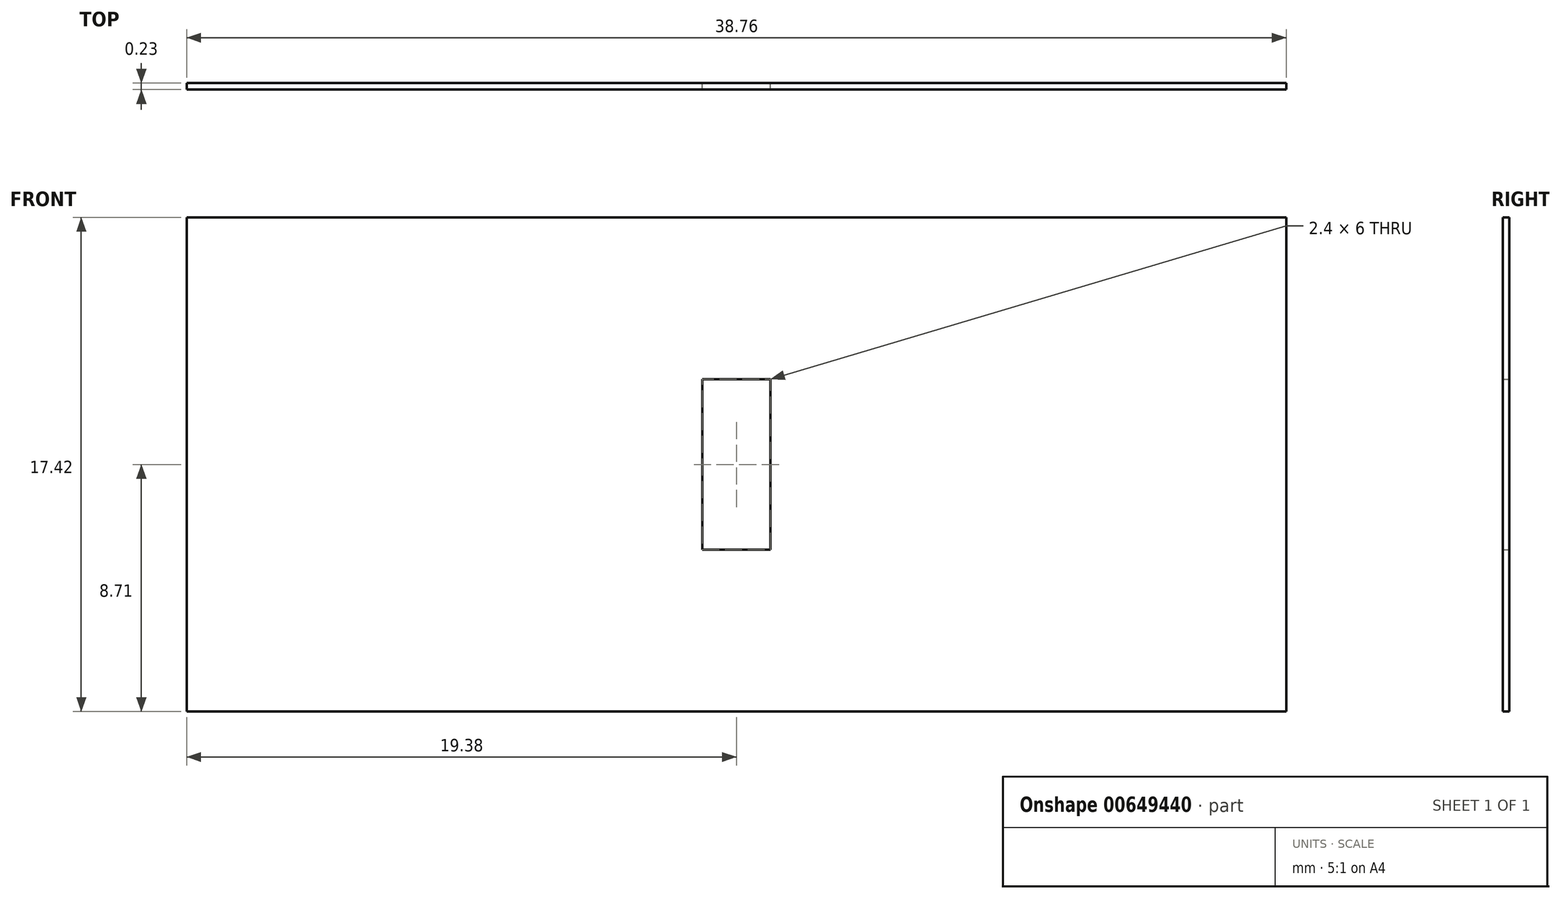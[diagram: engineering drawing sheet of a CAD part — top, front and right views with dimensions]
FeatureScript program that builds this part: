
annotation { "Feature Type Name" : "Feature", "Feature Type Description" : "" }
export const myFeature = defineFeature(function(context is Context, id is Id, definition is map)
    precondition{}
    {
        {
            var Q0;
            Q0=qCreatedBy(makeId("Front.planeOp"),FACE);
            var sketch = newSketch(context, id + "F0", { "sketchPlane" : qUnion([Q0])});
            skLineSegment(sketch, "E0.bottom", {"start": v(-19.38, 8.7) * mm, "end": v(19.38, 8.7) * mm});
            skLineSegment(sketch, "E0.top", {"start": v(-19.38, -8.7) * mm, "end": v(19.38, -8.7) * mm});
            skLineSegment(sketch, "E0.left", {"start": v(-19.38, 8.7) * mm, "end": v(-19.38, -8.7) * mm});
            skLineSegment(sketch, "E0.right", {"start": v(19.38, 8.7) * mm, "end": v(19.38, -8.7) * mm});
            skPoint(sketch, "E0.middle", {"position": v(0, 0) * mm});
            skLineSegment(sketch, "E1.bottom", {"start": v(1.2, -3) * mm, "end": v(-1.2, -3) * mm});
            skLineSegment(sketch, "E1.top", {"start": v(1.2, 3) * mm, "end": v(-1.2, 3) * mm});
            skLineSegment(sketch, "E1.left", {"start": v(1.2, -3) * mm, "end": v(1.2, 3) * mm});
            skLineSegment(sketch, "E1.right", {"start": v(-1.2, -3) * mm, "end": v(-1.2, 3) * mm});
            skSolve(sketch);
        }
        {
            var Q0;
            Q0=makeQuery(id+"F0.imprint","IMPRINT",FACE,{"disambiguationData":[TD([[makeQuery(id+"F0.imprint","IMPRINT",EDGE,{"derivedFrom":sQuery(id+"F0.wireOp",EDGE,"E0.bottom")}),-1.0]])]});
            extrude(context, id + "F1", {"entities" : qUnion([Q0]), "depth" : .23 * mm, "offsetDistance" : 25 * mm});
        }
    });
